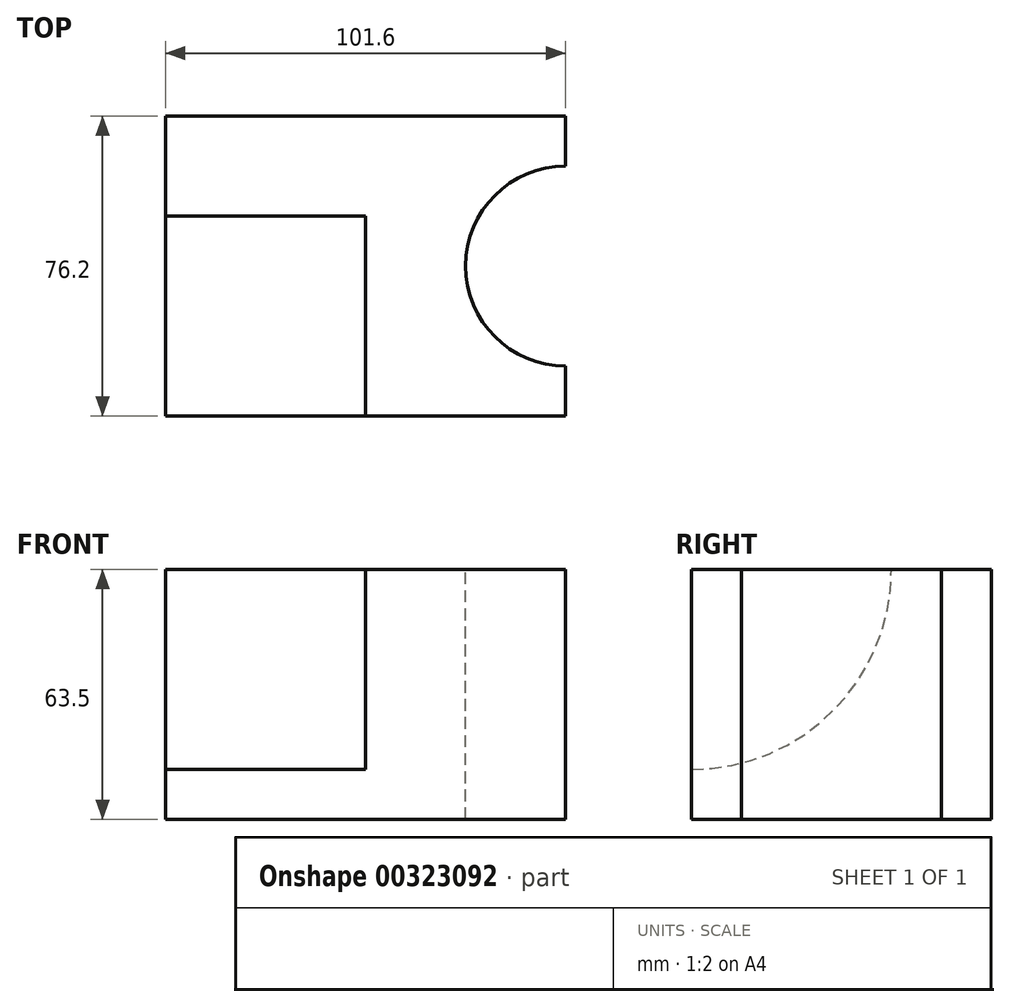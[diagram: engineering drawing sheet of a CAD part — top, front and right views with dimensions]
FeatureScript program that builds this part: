
annotation { "Feature Type Name" : "Feature", "Feature Type Description" : "" }
export const myFeature = defineFeature(function(context is Context, id is Id, definition is map)
    precondition{}
    {
        {
            var Q0;
            Q0=qCreatedBy(makeId("Front.planeOp"),FACE);
            var sketch = newSketch(context, id + "F0", { "sketchPlane" : qUnion([Q0])});
            skLineSegment(sketch, "E0", {"start": v(-49.05, -52.8) * mm, "end": v(52.55, -52.8) * mm});
            skLineSegment(sketch, "E1", {"start": v(52.55, -52.8) * mm, "end": v(52.55, 10.7) * mm});
            skLineSegment(sketch, "E2", {"start": v(52.55, 10.7) * mm, "end": v(-49.05, 10.7) * mm});
            skLineSegment(sketch, "E3", {"start": v(-49.05, 10.7) * mm, "end": v(-49.05, -52.8) * mm});
            skSolve(sketch);
        }
        {
            var Q0;
            Q0 = qSketchRegion(id + "F0", true);
            extrude(context, id + "F1", {"entities" : qUnion([Q0]), "depth" : 76.2 * mm});
        }
        {
            var Q0;
            Q0=makeQuery(id+"F1.opExtrude","SWEPT_FACE",FACE,{"disambiguationData":[OSD([sQuery(id+"F0.wireOp",EDGE,"E2")])]});
            var sketch = newSketch(context, id + "F2", { "sketchPlane" : qUnion([Q0])});
            skArc(sketch, "E4", {"start": v(52.55, -12.7) * mm, "mid": v(27.15, -38.1) * mm, "end": v(52.55, -63.5) * mm});
            skLineSegment(sketch, "E5", {"start": v(52.55, -12.7) * mm, "end": v(52.55, -63.5) * mm});
            skSolve(sketch);
        }
        {
            var Q0;
            Q0 = qSketchRegion(id + "F2", true);
            extrude(context, id + "F3", {"entities" : qUnion([Q0]), "operationType" : NewBodyOperationType.REMOVE, "endBound" : BoundingType.THROUGH_ALL, "oppositeDirection" : true, "depth" : 25.4 * mm});
        }
        {
            var Q0;
            Q0=makeQuery(id+"F1.opExtrude","SWEPT_FACE",FACE,{"disambiguationData":[OSD([sQuery(id+"F0.wireOp",EDGE,"E3")])]});
            var sketch = newSketch(context, id + "F4", { "sketchPlane" : qUnion([Q0])});
            skCircle(sketch, "E6", {"center": v(76.2, 10.7) * mm, "radius": 50.8 * mm});
            skSolve(sketch);
        }
        {
            var Q0;
            Q0 = qSketchRegion(id + "F4", true);
            extrude(context, id + "F5", {"entities" : qUnion([Q0]), "operationType" : NewBodyOperationType.REMOVE, "oppositeDirection" : true, "depth" : 50.8 * mm});
        }
    });
